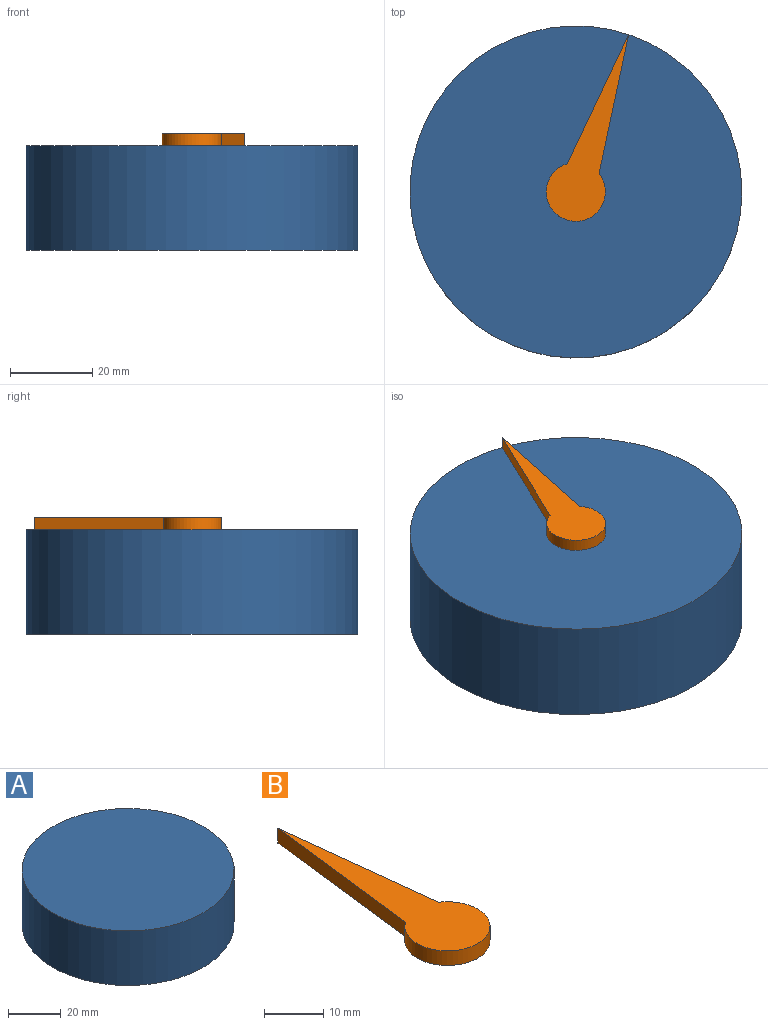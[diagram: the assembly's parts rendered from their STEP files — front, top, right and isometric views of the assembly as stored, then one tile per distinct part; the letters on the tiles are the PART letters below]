
ASSEMBLY  parts=2 mates=1
PART A: 3 faces, bbox 80.7x80.7x25.4 mm
  f0: cylinder r=40.33mm len=80.66mm, axis (0,0,-1), area 6436.4mm2, adj f1,f2
  f1: plane 80.66x80.66mm, normal (0,0,1), area 5109.9mm2, adj f0
  f2: plane 80.66x80.66mm, normal (0,0,-1), area 5109.9mm2, adj f0
PART B: 5 faces, bbox 14.3x47.5x3 mm
  f0: cylinder r=7.17mm len=14.34mm, axis (0,0,-1), area 109.4mm2, adj f1,f2,f3,f4
  f1: plane 34.33x3.93mm, normal (0.99,0.11,0), area 103.7mm2, adj f0,f2,f3,f4
  f2: plane 34.48x4.15mm, normal (-0.99,0.12,0), area 104.2mm2, adj f0,f1,f3,f4
  f3: plane 47.5x14.34mm, normal (0,0,1), area 293.7mm2, adj f0,f1,f2
  f4: plane 47.5x14.34mm, normal (0,0,-1), area 293.7mm2, adj f0,f1,f2
PLACE A at identity fixed
PLACE B rot(axis=(0,0,-1),18.6deg) t=(0,0,0)mm
MATE revolute A.f0 <-> B.f0  axis (0,0,1) through (0,0,25.4)mm
